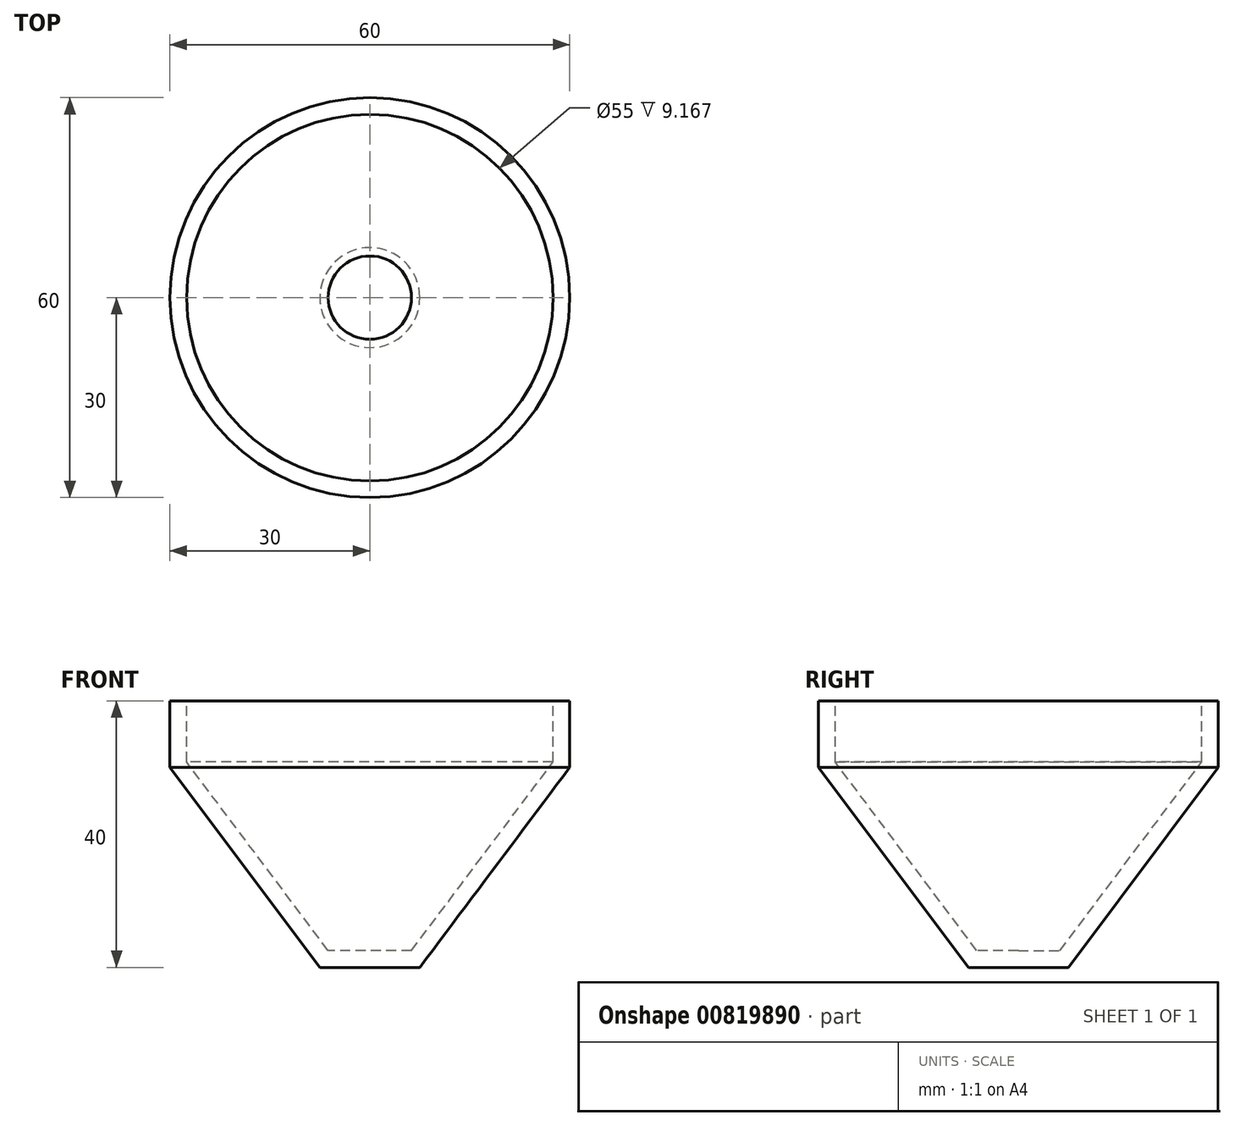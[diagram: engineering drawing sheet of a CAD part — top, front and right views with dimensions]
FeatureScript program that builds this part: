
annotation { "Feature Type Name" : "Feature", "Feature Type Description" : "" }
export const myFeature = defineFeature(function(context is Context, id is Id, definition is map)
    precondition{}
    {
        {
            var Q0;
            Q0=qCreatedBy(makeId("Front.planeOp"),FACE);
            var sketch = newSketch(context, id + "F0", { "sketchPlane" : qUnion([Q0])});
            skLineSegment(sketch, "E0", {"start": v(-30, 30) * mm, "end": v(-30, 40) * mm});
            skLineSegment(sketch, "E1", {"start": v(-30, 40) * mm, "end": v(0, 40) * mm});
            skLineSegment(sketch, "E2", {"start": v(0, 40) * mm, "end": v(0, 0) * mm});
            skLineSegment(sketch, "E3", {"start": v(-30, 30) * mm, "end": v(-7.5, 0) * mm});
            skLineSegment(sketch, "E4", {"start": v(-7.5, 0) * mm, "end": v(0, 0) * mm});
            skSolve(sketch);
        }
        {
            var Q0;
            Q0=makeQuery(id+"F0.imprint","IMPRINT",FACE,{"disambiguationData":[TD([[makeQuery(id+"F0.imprint","IMPRINT",EDGE,{"derivedFrom":sQuery(id+"F0.wireOp",EDGE,"E0")}),-1.0]])]});
            var Q1;
            Q1=sQuery(id+"F0.wireOp",EDGE,"E2");
            revolve(context, id + "F1", {"surfaceOperationType" : NewSurfaceOperationType.NEW, "entities" : qUnion([Q0]), "axis" : qUnion([Q1]), "revolveType" : RevolveType.FULL});
        }
        {
            var Q0;
            Q0=makeQuery(id+"F1.opRevolve","SWEPT_FACE",FACE,{"disambiguationData":[OSD([sQuery(id+"F0.wireOp",EDGE,"E1")])]});
            shell(context, id + "F2", {"entities" : qUnion([Q0]), "thickness" : 2.5 * mm});
        }
    });
